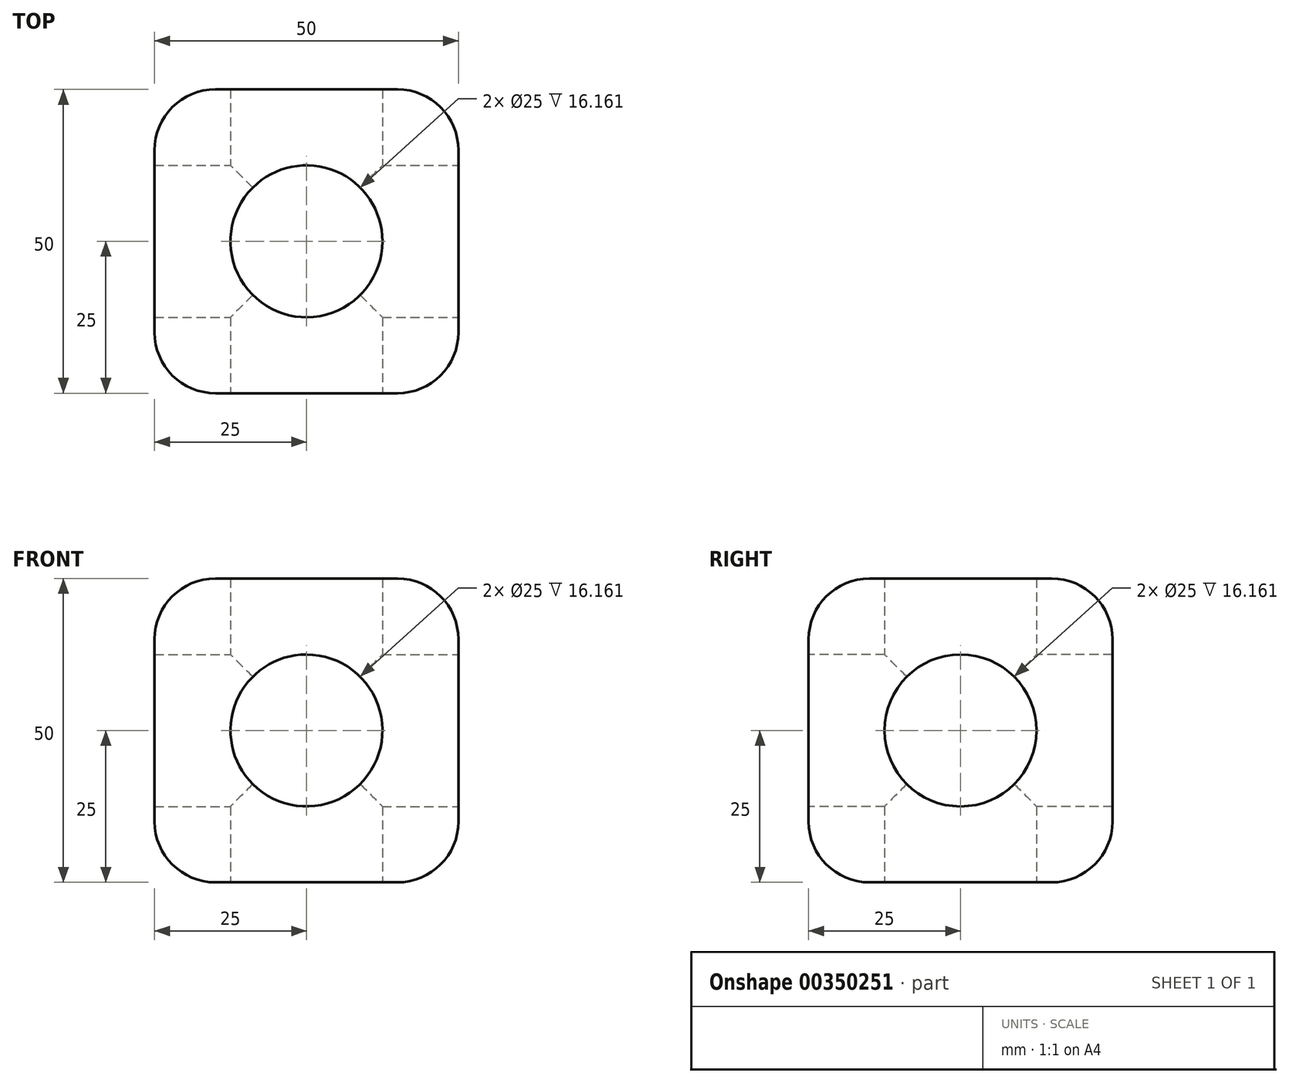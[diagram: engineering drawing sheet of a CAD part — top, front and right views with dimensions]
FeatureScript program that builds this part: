
annotation { "Feature Type Name" : "Feature", "Feature Type Description" : "" }
export const myFeature = defineFeature(function(context is Context, id is Id, definition is map)
    precondition{}
    {
        {
            var Q0;
            Q0=qCreatedBy(makeId("Top.planeOp"),FACE);
            var sketch = newSketch(context, id + "F0", { "sketchPlane" : qUnion([Q0])});
            skLineSegment(sketch, "E0", {"start": v(-25, 25) * mm, "end": v(25, 25) * mm});
            skLineSegment(sketch, "E1", {"start": v(25, 25) * mm, "end": v(25, 25) * mm});
            skLineSegment(sketch, "E2", {"start": v(25, 25) * mm, "end": v(25, -25) * mm});
            skLineSegment(sketch, "E3", {"start": v(25, -25) * mm, "end": v(25, -25) * mm});
            skLineSegment(sketch, "E4", {"start": v(-25, -25) * mm, "end": v(25, -25) * mm});
            skLineSegment(sketch, "E5", {"start": v(-25, -25) * mm, "end": v(-25, 25) * mm});
            skSolve(sketch);
        }
        {
            var Q0;
            Q0=makeQuery(id+"F0.imprint","IMPRINT",FACE,{"disambiguationData":[TD([[makeQuery(id+"F0.imprint","IMPRINT",EDGE,{"derivedFrom":sQuery(id+"F0.wireOp",EDGE,"E0")}),-1.0]])]});
            extrude(context, id + "F1", {"entities" : qUnion([Q0]), "depth" : 50 * mm});
        }
        {
            var Q0;
            Q0=qCreatedBy(makeId("Top.planeOp"),FACE);
            var sketch = newSketch(context, id + "F2", { "sketchPlane" : qUnion([Q0])});
            skCircle(sketch, "E6", {"center": v(0, 0) * mm, "radius": 12.5 * mm});
            skSolve(sketch);
        }
        {
            var Q0;
            Q0=makeQuery(id+"F2.imprint","IMPRINT",FACE,{"disambiguationData":[TD([[makeQuery(id+"F2.imprint","IMPRINT",EDGE,{"derivedFrom":sQuery(id+"F2.wireOp",EDGE,"E6")}),1.0]])]});
            var Q1;
            Q1=sQuery(id+"F2.wireOp",EDGE,"E6");
            extrude(context, id + "F3", {"entities" : qUnion([Q0]), "operationType" : NewBodyOperationType.REMOVE, "surfaceEntities" : qUnion([Q1]), "depth" : 213.37 * mm});
        }
        {
            var Q0;
            Q0=makeQuery(id+"F1.opExtrude","SWEPT_EDGE",EDGE,{"disambiguationData":[OSD([sQuery(id+"F0.wireOp",EDGE,"E2"),sQuery(id+"F0.wireOp",EDGE,"E4")])]});
            var Q1;
            Q1=makeQuery(id+"F1.opExtrude","CAP_EDGE",EDGE,{"disambiguationData":[OSD([sQuery(id+"F0.wireOp",EDGE,"E2")])],"isStart":false});
            var Q2;
            Q2=makeQuery(id+"F1.opExtrude","SWEPT_EDGE",EDGE,{"disambiguationData":[OSD([sQuery(id+"F0.wireOp",EDGE,"E0"),sQuery(id+"F0.wireOp",EDGE,"E2")])]});
            var Q3;
            Q3=makeQuery(id+"F1.opExtrude","CAP_EDGE",EDGE,{"disambiguationData":[OSD([sQuery(id+"F0.wireOp",EDGE,"E2")])],"isStart":true});
            var Q4;
            Q4=makeQuery(id+"F1.opExtrude","CAP_EDGE",EDGE,{"disambiguationData":[OSD([sQuery(id+"F0.wireOp",EDGE,"E0")])],"isStart":false});
            var Q5;
            Q5=makeQuery(id+"F1.opExtrude","CAP_EDGE",EDGE,{"disambiguationData":[OSD([sQuery(id+"F0.wireOp",EDGE,"E4")])],"isStart":false});
            var Q6;
            Q6=makeQuery(id+"F1.opExtrude","CAP_EDGE",EDGE,{"disambiguationData":[OSD([sQuery(id+"F0.wireOp",EDGE,"E5")])],"isStart":false});
            var Q7;
            Q7=makeQuery(id+"F1.opExtrude","SWEPT_EDGE",EDGE,{"disambiguationData":[OSD([sQuery(id+"F0.wireOp",EDGE,"E4"),sQuery(id+"F0.wireOp",EDGE,"E5")])]});
            var Q8;
            Q8=makeQuery(id+"F1.opExtrude","CAP_EDGE",EDGE,{"disambiguationData":[OSD([sQuery(id+"F0.wireOp",EDGE,"E4")])],"isStart":true});
            var Q9;
            Q9=makeQuery(id+"F1.opExtrude","CAP_EDGE",EDGE,{"disambiguationData":[OSD([sQuery(id+"F0.wireOp",EDGE,"E5")])],"isStart":true});
            var Q10;
            Q10=makeQuery(id+"F1.opExtrude","CAP_EDGE",EDGE,{"disambiguationData":[OSD([sQuery(id+"F0.wireOp",EDGE,"E0")])],"isStart":true});
            var Q11;
            Q11=makeQuery(id+"F1.opExtrude","SWEPT_EDGE",EDGE,{"disambiguationData":[OSD([sQuery(id+"F0.wireOp",EDGE,"E0"),sQuery(id+"F0.wireOp",EDGE,"E5")])]});
            fillet(context, id + "F4", {"entities" : qUnion([Q0, Q1, Q2, Q3, Q4, Q5, Q6, Q7, Q8, Q9, Q10, Q11]), "radius" : 10 * mm, "tangentPropagation" : true, "allowEdgeOverflow" : false});
        }
        {
            var Q0;
            Q0=qCreatedBy(makeId("Right.planeOp"),FACE);
            var sketch = newSketch(context, id + "F5", { "sketchPlane" : qUnion([Q0])});
            skCircle(sketch, "E7", {"center": v(0, 25) * mm, "radius": 12.5 * mm});
            skSolve(sketch);
        }
        {
            var Q0;
            Q0 = qSketchRegion(id + "F5", true);
            extrude(context, id + "F6", {"entities" : qUnion([Q0]), "operationType" : NewBodyOperationType.REMOVE, "endBound" : BoundingType.SYMMETRIC, "oppositeDirection" : true, "depth" : 100 * mm});
        }
        {
            var Q0;
            Q0=qCreatedBy(makeId("Front.planeOp"),FACE);
            var sketch = newSketch(context, id + "F7", { "sketchPlane" : qUnion([Q0])});
            skCircle(sketch, "E8", {"center": v(0, 25) * mm, "radius": 12.5 * mm});
            skSolve(sketch);
        }
        {
            var Q0;
            Q0 = qSketchRegion(id + "F7", true);
            extrude(context, id + "F8", {"entities" : qUnion([Q0]), "operationType" : NewBodyOperationType.REMOVE, "endBound" : BoundingType.SYMMETRIC, "oppositeDirection" : true, "depth" : 100 * mm});
        }
    });
